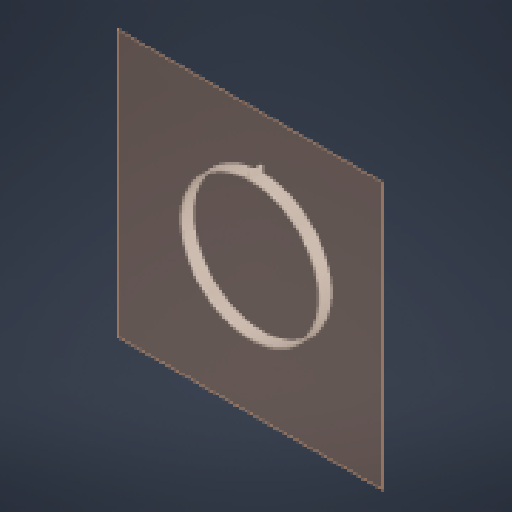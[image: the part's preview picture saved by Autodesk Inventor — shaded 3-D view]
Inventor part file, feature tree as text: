
AUTODESK INVENTOR PART (.ipt)
format: ipt  version: 2023.1 (Build 271208000, 208)  size: 183,296 bytes
history: native  units: mm
features: other x3, plane x1, extrude x1, sketch x1
ambient origin geometry x8: Origin, YZ Plane, XZ Plane, XY Plane, X Axis, Y Axis, Z Axis, Center Point
bodies: Solid1 (feature_tree)
feature tree (6):
  plane  "Work Plane1"
  extrude  "Extrusion1"  Depth=2.0mm
  sketch  "Sketch1"  dims[d0=170.0mm d1=2.0mm d2=1.0mm d3=10.0mm d4=1.0mm d5=15.0mm d6=0.0mm]
  parser-record x1  (decoder bookkeeping rows leaked as tree rows — omitted from the tree; the rows remain in map.json)
  other  "Beau4tClock.iam"
  other  "Clock:1"
note: 1 file-system path scrubbed to <path> (originals preserved in map.json)
